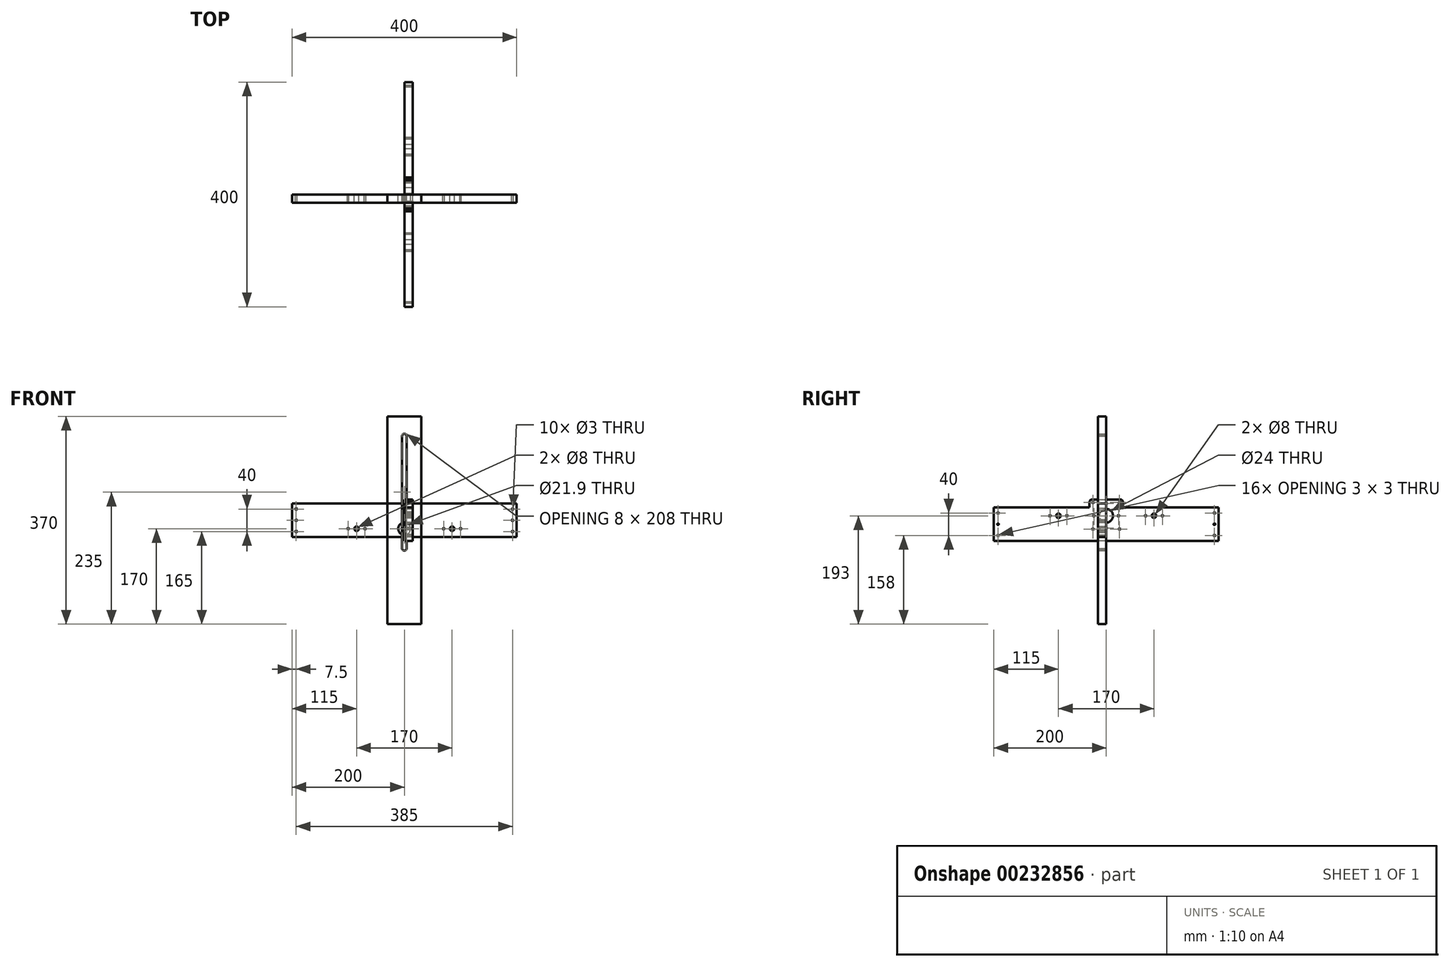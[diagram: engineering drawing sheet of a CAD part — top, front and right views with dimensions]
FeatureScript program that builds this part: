
annotation { "Feature Type Name" : "Feature", "Feature Type Description" : "" }
export const myFeature = defineFeature(function(context is Context, id is Id, definition is map)
    precondition{}
    {
        {
            var Q0;
            Q0=qCreatedBy(makeId("Front.planeOp"),FACE);
            var sketch = newSketch(context, id + "F0", { "sketchPlane" : qUnion([Q0])});
            skLineSegment(sketch, "E0", {"start": v(-200, 30) * mm, "end": v(200, 30) * mm});
            skLineSegment(sketch, "E1", {"start": v(200, 30) * mm, "end": v(200, -30) * mm});
            skLineSegment(sketch, "E2", {"start": v(200, -30) * mm, "end": v(-200, -30) * mm});
            skLineSegment(sketch, "E3", {"start": v(-200, -30) * mm, "end": v(-200, 30) * mm});
            skCircle(sketch, "E4", {"center": v(0, -15) * mm, "radius": 10.95 * mm});
            skCircle(sketch, "E5", {"center": v(-100, -15) * mm, "radius": 1.5 * mm});
            skCircle(sketch, "E6", {"center": v(-70, -15) * mm, "radius": 1.5 * mm});
            skCircle(sketch, "E7", {"center": v(-192.5, -20) * mm, "radius": 1.5 * mm});
            skCircle(sketch, "E8", {"center": v(-192.5, 20) * mm, "radius": 1.5 * mm});
            skCircle(sketch, "E9", {"center": v(-192.5, 0) * mm, "radius": 1.5 * mm});
            skCircle(sketch, "E10", {"center": v(70, -15) * mm, "radius": 1.5 * mm});
            skCircle(sketch, "E11", {"center": v(85, -15) * mm, "radius": 4 * mm});
            skCircle(sketch, "E12", {"center": v(100, -15) * mm, "radius": 1.5 * mm});
            skCircle(sketch, "E13", {"center": v(192.5, -20) * mm, "radius": 1.5 * mm});
            skCircle(sketch, "E14", {"center": v(192.5, 0) * mm, "radius": 1.5 * mm});
            skCircle(sketch, "E15", {"center": v(192.5, 20) * mm, "radius": 1.5 * mm});
            skCircle(sketch, "E16", {"center": v(-85, -15) * mm, "radius": 4 * mm});
            skSolve(sketch);
        }
        {
            var Q0;
            Q0=makeQuery(id+"F0.imprint","IMPRINT",FACE,{"disambiguationData":[TD([[makeQuery(id+"F0.imprint","IMPRINT",EDGE,{"derivedFrom":sQuery(id+"F0.wireOp",EDGE,"E0")}),-1.0]])]});
            extrude(context, id + "F1", {"entities" : qUnion([Q0]), "depth" : 15 * mm});
        }
        {
            var Q0;
            Q0=qCreatedBy(makeId("Right.planeOp"),FACE);
            var sketch = newSketch(context, id + "F2", { "sketchPlane" : qUnion([Q0])});
            skLineSegment(sketch, "E17", {"start": v(-30, 23) * mm, "end": v(-30, 32) * mm});
            skLineSegment(sketch, "E18", {"start": v(-30, 32) * mm, "end": v(-29.96, 32.65) * mm});
            skLineSegment(sketch, "E19", {"start": v(-29.96, 32.65) * mm, "end": v(-29.83, 33.3) * mm});
            skLineSegment(sketch, "E20", {"start": v(-29.83, 33.3) * mm, "end": v(-29.62, 33.91) * mm});
            skLineSegment(sketch, "E21", {"start": v(-29.62, 33.91) * mm, "end": v(-29.33, 34.5) * mm});
            skLineSegment(sketch, "E22", {"start": v(-29.33, 34.5) * mm, "end": v(-28.97, 35.04) * mm});
            skLineSegment(sketch, "E23", {"start": v(-28.97, 35.04) * mm, "end": v(-28.54, 35.54) * mm});
            skLineSegment(sketch, "E24", {"start": v(-28.54, 35.54) * mm, "end": v(-28.04, 35.97) * mm});
            skLineSegment(sketch, "E25", {"start": v(-28.04, 35.97) * mm, "end": v(-27.5, 36.33) * mm});
            skLineSegment(sketch, "E26", {"start": v(-27.5, 36.33) * mm, "end": v(-26.91, 36.62) * mm});
            skLineSegment(sketch, "E27", {"start": v(-26.91, 36.62) * mm, "end": v(-26.3, 36.83) * mm});
            skLineSegment(sketch, "E28", {"start": v(-26.3, 36.83) * mm, "end": v(-25.65, 36.96) * mm});
            skLineSegment(sketch, "E29", {"start": v(-25.65, 36.96) * mm, "end": v(-25, 37) * mm});
            skLineSegment(sketch, "E30", {"start": v(-25, 37) * mm, "end": v(25, 37) * mm});
            skLineSegment(sketch, "E31", {"start": v(25, 37) * mm, "end": v(25.65, 36.96) * mm});
            skLineSegment(sketch, "E32", {"start": v(25.65, 36.96) * mm, "end": v(26.3, 36.83) * mm});
            skLineSegment(sketch, "E33", {"start": v(26.3, 36.83) * mm, "end": v(26.91, 36.62) * mm});
            skLineSegment(sketch, "E34", {"start": v(26.91, 36.62) * mm, "end": v(27.5, 36.33) * mm});
            skLineSegment(sketch, "E35", {"start": v(27.5, 36.33) * mm, "end": v(28.04, 35.97) * mm});
            skLineSegment(sketch, "E36", {"start": v(28.04, 35.97) * mm, "end": v(28.54, 35.54) * mm});
            skLineSegment(sketch, "E37", {"start": v(28.54, 35.54) * mm, "end": v(28.97, 35.04) * mm});
            skLineSegment(sketch, "E38", {"start": v(28.97, 35.04) * mm, "end": v(29.33, 34.5) * mm});
            skLineSegment(sketch, "E39", {"start": v(29.33, 34.5) * mm, "end": v(29.62, 33.91) * mm});
            skLineSegment(sketch, "E40", {"start": v(29.62, 33.91) * mm, "end": v(29.83, 33.3) * mm});
            skLineSegment(sketch, "E41", {"start": v(29.83, 33.3) * mm, "end": v(29.96, 32.65) * mm});
            skLineSegment(sketch, "E42", {"start": v(29.96, 32.65) * mm, "end": v(30, 32) * mm});
            skLineSegment(sketch, "E43", {"start": v(30, 32) * mm, "end": v(30, 23) * mm});
            skLineSegment(sketch, "E44", {"start": v(30, 23) * mm, "end": v(200, 23) * mm});
            skLineSegment(sketch, "E45", {"start": v(200, 23) * mm, "end": v(200, -37) * mm});
            skLineSegment(sketch, "E46", {"start": v(200, -37) * mm, "end": v(-200, -37) * mm});
            skLineSegment(sketch, "E47", {"start": v(-200, -37) * mm, "end": v(-200, 23) * mm});
            skLineSegment(sketch, "E48", {"start": v(-200, 23) * mm, "end": v(-30, 23) * mm});
            skLineSegment(sketch, "E49", {"start": v(-0.39, -12.47) * mm, "end": v(-0.75, -12.62) * mm});
            skLineSegment(sketch, "E50", {"start": v(-0.75, -12.62) * mm, "end": v(-1.06, -12.86) * mm});
            skLineSegment(sketch, "E51", {"start": v(-1.06, -12.86) * mm, "end": v(-1.3, -13.17) * mm});
            skLineSegment(sketch, "E52", {"start": v(-1.3, -13.17) * mm, "end": v(-1.45, -13.53) * mm});
            skLineSegment(sketch, "E53", {"start": v(-1.45, -13.53) * mm, "end": v(-1.5, -13.92) * mm});
            skLineSegment(sketch, "E54", {"start": v(-1.5, -13.92) * mm, "end": v(-1.45, -14.3) * mm});
            skLineSegment(sketch, "E55", {"start": v(-1.45, -14.3) * mm, "end": v(-1.3, -14.67) * mm});
            skLineSegment(sketch, "E56", {"start": v(-1.3, -14.67) * mm, "end": v(-1.06, -14.98) * mm});
            skLineSegment(sketch, "E57", {"start": v(-1.06, -14.98) * mm, "end": v(-0.75, -15.22) * mm});
            skLineSegment(sketch, "E58", {"start": v(-0.75, -15.22) * mm, "end": v(-0.39, -15.37) * mm});
            skLineSegment(sketch, "E59", {"start": v(-0.39, -15.37) * mm, "end": v(0, -15.42) * mm});
            skLineSegment(sketch, "E60", {"start": v(0, -15.42) * mm, "end": v(0.39, -15.37) * mm});
            skLineSegment(sketch, "E61", {"start": v(0.39, -15.37) * mm, "end": v(0.75, -15.22) * mm});
            skLineSegment(sketch, "E62", {"start": v(0.75, -15.22) * mm, "end": v(1.06, -14.98) * mm});
            skLineSegment(sketch, "E63", {"start": v(1.06, -14.98) * mm, "end": v(1.3, -14.67) * mm});
            skLineSegment(sketch, "E64", {"start": v(1.3, -14.67) * mm, "end": v(1.45, -14.3) * mm});
            skLineSegment(sketch, "E65", {"start": v(1.45, -14.3) * mm, "end": v(1.5, -13.92) * mm});
            skLineSegment(sketch, "E66", {"start": v(1.5, -13.92) * mm, "end": v(1.45, -13.53) * mm});
            skLineSegment(sketch, "E67", {"start": v(1.45, -13.53) * mm, "end": v(1.3, -13.17) * mm});
            skLineSegment(sketch, "E68", {"start": v(1.3, -13.17) * mm, "end": v(1.06, -12.86) * mm});
            skLineSegment(sketch, "E69", {"start": v(1.06, -12.86) * mm, "end": v(0.75, -12.62) * mm});
            skLineSegment(sketch, "E70", {"start": v(0.75, -12.62) * mm, "end": v(0.39, -12.47) * mm});
            skLineSegment(sketch, "E71", {"start": v(0.39, -12.47) * mm, "end": v(0, -12.42) * mm});
            skLineSegment(sketch, "E72", {"start": v(0, -12.42) * mm, "end": v(-0.39, -12.47) * mm});
            skLineSegment(sketch, "E73", {"start": v(21.17, 9.3) * mm, "end": v(20.86, 9.06) * mm});
            skLineSegment(sketch, "E74", {"start": v(20.86, 9.06) * mm, "end": v(20.62, 8.75) * mm});
            skLineSegment(sketch, "E75", {"start": v(20.62, 8.75) * mm, "end": v(20.47, 8.39) * mm});
            skLineSegment(sketch, "E76", {"start": v(20.47, 8.39) * mm, "end": v(20.42, 8) * mm});
            skLineSegment(sketch, "E77", {"start": v(20.42, 8) * mm, "end": v(20.47, 7.61) * mm});
            skLineSegment(sketch, "E78", {"start": v(20.47, 7.61) * mm, "end": v(20.62, 7.25) * mm});
            skLineSegment(sketch, "E79", {"start": v(20.62, 7.25) * mm, "end": v(20.86, 6.94) * mm});
            skLineSegment(sketch, "E80", {"start": v(20.86, 6.94) * mm, "end": v(21.17, 6.7) * mm});
            skLineSegment(sketch, "E81", {"start": v(21.17, 6.7) * mm, "end": v(21.53, 6.55) * mm});
            skLineSegment(sketch, "E82", {"start": v(21.53, 6.55) * mm, "end": v(21.92, 6.5) * mm});
            skLineSegment(sketch, "E83", {"start": v(21.92, 6.5) * mm, "end": v(22.3, 6.55) * mm});
            skLineSegment(sketch, "E84", {"start": v(22.3, 6.55) * mm, "end": v(22.67, 6.7) * mm});
            skLineSegment(sketch, "E85", {"start": v(22.67, 6.7) * mm, "end": v(22.98, 6.94) * mm});
            skLineSegment(sketch, "E86", {"start": v(22.98, 6.94) * mm, "end": v(23.22, 7.25) * mm});
            skLineSegment(sketch, "E87", {"start": v(23.22, 7.25) * mm, "end": v(23.37, 7.61) * mm});
            skLineSegment(sketch, "E88", {"start": v(23.37, 7.61) * mm, "end": v(23.42, 8) * mm});
            skLineSegment(sketch, "E89", {"start": v(23.42, 8) * mm, "end": v(23.37, 8.39) * mm});
            skLineSegment(sketch, "E90", {"start": v(23.37, 8.39) * mm, "end": v(23.22, 8.75) * mm});
            skLineSegment(sketch, "E91", {"start": v(23.22, 8.75) * mm, "end": v(22.98, 9.06) * mm});
            skLineSegment(sketch, "E92", {"start": v(22.98, 9.06) * mm, "end": v(22.67, 9.3) * mm});
            skLineSegment(sketch, "E93", {"start": v(22.67, 9.3) * mm, "end": v(22.3, 9.45) * mm});
            skLineSegment(sketch, "E94", {"start": v(22.3, 9.45) * mm, "end": v(21.92, 9.5) * mm});
            skLineSegment(sketch, "E95", {"start": v(21.92, 9.5) * mm, "end": v(21.53, 9.45) * mm});
            skLineSegment(sketch, "E96", {"start": v(21.53, 9.45) * mm, "end": v(21.17, 9.3) * mm});
            skLineSegment(sketch, "E97", {"start": v(-22.98, 9.06) * mm, "end": v(-23.22, 8.75) * mm});
            skLineSegment(sketch, "E98", {"start": v(-23.22, 8.75) * mm, "end": v(-23.37, 8.39) * mm});
            skLineSegment(sketch, "E99", {"start": v(-23.37, 8.39) * mm, "end": v(-23.42, 8) * mm});
            skLineSegment(sketch, "E100", {"start": v(-23.42, 8) * mm, "end": v(-23.37, 7.61) * mm});
            skLineSegment(sketch, "E101", {"start": v(-23.37, 7.61) * mm, "end": v(-23.22, 7.25) * mm});
            skLineSegment(sketch, "E102", {"start": v(-23.22, 7.25) * mm, "end": v(-22.98, 6.94) * mm});
            skLineSegment(sketch, "E103", {"start": v(-22.98, 6.94) * mm, "end": v(-22.67, 6.7) * mm});
            skLineSegment(sketch, "E104", {"start": v(-22.67, 6.7) * mm, "end": v(-22.3, 6.55) * mm});
            skLineSegment(sketch, "E105", {"start": v(-22.3, 6.55) * mm, "end": v(-21.92, 6.5) * mm});
            skLineSegment(sketch, "E106", {"start": v(-21.92, 6.5) * mm, "end": v(-21.53, 6.55) * mm});
            skLineSegment(sketch, "E107", {"start": v(-21.53, 6.55) * mm, "end": v(-21.17, 6.7) * mm});
            skLineSegment(sketch, "E108", {"start": v(-21.17, 6.7) * mm, "end": v(-20.86, 6.94) * mm});
            skLineSegment(sketch, "E109", {"start": v(-20.86, 6.94) * mm, "end": v(-20.62, 7.25) * mm});
            skLineSegment(sketch, "E110", {"start": v(-20.62, 7.25) * mm, "end": v(-20.47, 7.61) * mm});
            skLineSegment(sketch, "E111", {"start": v(-20.47, 7.61) * mm, "end": v(-20.42, 8) * mm});
            skLineSegment(sketch, "E112", {"start": v(-20.42, 8) * mm, "end": v(-20.47, 8.39) * mm});
            skLineSegment(sketch, "E113", {"start": v(-20.47, 8.39) * mm, "end": v(-20.62, 8.75) * mm});
            skLineSegment(sketch, "E114", {"start": v(-20.62, 8.75) * mm, "end": v(-20.86, 9.06) * mm});
            skLineSegment(sketch, "E115", {"start": v(-20.86, 9.06) * mm, "end": v(-21.17, 9.3) * mm});
            skLineSegment(sketch, "E116", {"start": v(-21.17, 9.3) * mm, "end": v(-21.53, 9.45) * mm});
            skLineSegment(sketch, "E117", {"start": v(-21.53, 9.45) * mm, "end": v(-21.92, 9.5) * mm});
            skLineSegment(sketch, "E118", {"start": v(-21.92, 9.5) * mm, "end": v(-22.3, 9.45) * mm});
            skLineSegment(sketch, "E119", {"start": v(-22.3, 9.45) * mm, "end": v(-22.67, 9.3) * mm});
            skLineSegment(sketch, "E120", {"start": v(-22.67, 9.3) * mm, "end": v(-22.98, 9.06) * mm});
            skLineSegment(sketch, "E121", {"start": v(-1.3, 29.17) * mm, "end": v(-1.06, 28.86) * mm});
            skLineSegment(sketch, "E122", {"start": v(-1.06, 28.86) * mm, "end": v(-0.75, 28.62) * mm});
            skLineSegment(sketch, "E123", {"start": v(-0.75, 28.62) * mm, "end": v(-0.39, 28.47) * mm});
            skLineSegment(sketch, "E124", {"start": v(-0.39, 28.47) * mm, "end": v(0, 28.42) * mm});
            skLineSegment(sketch, "E125", {"start": v(0, 28.42) * mm, "end": v(0.39, 28.47) * mm});
            skLineSegment(sketch, "E126", {"start": v(0.39, 28.47) * mm, "end": v(0.75, 28.62) * mm});
            skLineSegment(sketch, "E127", {"start": v(0.75, 28.62) * mm, "end": v(1.06, 28.86) * mm});
            skLineSegment(sketch, "E128", {"start": v(1.06, 28.86) * mm, "end": v(1.3, 29.17) * mm});
            skLineSegment(sketch, "E129", {"start": v(1.3, 29.17) * mm, "end": v(1.45, 29.53) * mm});
            skLineSegment(sketch, "E130", {"start": v(1.45, 29.53) * mm, "end": v(1.5, 29.92) * mm});
            skLineSegment(sketch, "E131", {"start": v(1.5, 29.92) * mm, "end": v(1.45, 30.3) * mm});
            skLineSegment(sketch, "E132", {"start": v(1.45, 30.3) * mm, "end": v(1.3, 30.67) * mm});
            skLineSegment(sketch, "E133", {"start": v(1.3, 30.67) * mm, "end": v(1.06, 30.98) * mm});
            skLineSegment(sketch, "E134", {"start": v(1.06, 30.98) * mm, "end": v(0.75, 31.22) * mm});
            skLineSegment(sketch, "E135", {"start": v(0.75, 31.22) * mm, "end": v(0.39, 31.37) * mm});
            skLineSegment(sketch, "E136", {"start": v(0.39, 31.37) * mm, "end": v(0, 31.42) * mm});
            skLineSegment(sketch, "E137", {"start": v(0, 31.42) * mm, "end": v(-0.39, 31.37) * mm});
            skLineSegment(sketch, "E138", {"start": v(-0.39, 31.37) * mm, "end": v(-0.75, 31.22) * mm});
            skLineSegment(sketch, "E139", {"start": v(-0.75, 31.22) * mm, "end": v(-1.06, 30.98) * mm});
            skLineSegment(sketch, "E140", {"start": v(-1.06, 30.98) * mm, "end": v(-1.3, 30.67) * mm});
            skLineSegment(sketch, "E141", {"start": v(-1.3, 30.67) * mm, "end": v(-1.45, 30.3) * mm});
            skLineSegment(sketch, "E142", {"start": v(-1.45, 30.3) * mm, "end": v(-1.5, 29.92) * mm});
            skLineSegment(sketch, "E143", {"start": v(-1.5, 29.92) * mm, "end": v(-1.45, 29.53) * mm});
            skLineSegment(sketch, "E144", {"start": v(-1.45, 29.53) * mm, "end": v(-1.3, 29.17) * mm});
            skLineSegment(sketch, "E145", {"start": v(23.94, -14.1) * mm, "end": v(23.55, -14.05) * mm});
            skLineSegment(sketch, "E146", {"start": v(23.55, -14.05) * mm, "end": v(23.16, -14.1) * mm});
            skLineSegment(sketch, "E147", {"start": v(23.16, -14.1) * mm, "end": v(22.8, -14.25) * mm});
            skLineSegment(sketch, "E148", {"start": v(22.8, -14.25) * mm, "end": v(22.49, -14.49) * mm});
            skLineSegment(sketch, "E149", {"start": v(22.49, -14.49) * mm, "end": v(22.25, -14.8) * mm});
            skLineSegment(sketch, "E150", {"start": v(22.25, -14.8) * mm, "end": v(22.1, -15.16) * mm});
            skLineSegment(sketch, "E151", {"start": v(22.1, -15.16) * mm, "end": v(22.05, -15.55) * mm});
            skLineSegment(sketch, "E152", {"start": v(22.05, -15.55) * mm, "end": v(22.1, -15.94) * mm});
            skLineSegment(sketch, "E153", {"start": v(22.1, -15.94) * mm, "end": v(22.25, -16.3) * mm});
            skLineSegment(sketch, "E154", {"start": v(22.25, -16.3) * mm, "end": v(22.49, -16.61) * mm});
            skLineSegment(sketch, "E155", {"start": v(22.49, -16.61) * mm, "end": v(22.8, -16.85) * mm});
            skLineSegment(sketch, "E156", {"start": v(22.8, -16.85) * mm, "end": v(23.16, -17) * mm});
            skLineSegment(sketch, "E157", {"start": v(23.16, -17) * mm, "end": v(23.55, -17.05) * mm});
            skLineSegment(sketch, "E158", {"start": v(23.55, -17.05) * mm, "end": v(23.94, -17) * mm});
            skLineSegment(sketch, "E159", {"start": v(23.94, -17) * mm, "end": v(24.3, -16.85) * mm});
            skLineSegment(sketch, "E160", {"start": v(24.3, -16.85) * mm, "end": v(24.61, -16.61) * mm});
            skLineSegment(sketch, "E161", {"start": v(24.61, -16.61) * mm, "end": v(24.85, -16.3) * mm});
            skLineSegment(sketch, "E162", {"start": v(24.85, -16.3) * mm, "end": v(25, -15.94) * mm});
            skLineSegment(sketch, "E163", {"start": v(25, -15.94) * mm, "end": v(25.05, -15.55) * mm});
            skLineSegment(sketch, "E164", {"start": v(25.05, -15.55) * mm, "end": v(25, -15.16) * mm});
            skLineSegment(sketch, "E165", {"start": v(25, -15.16) * mm, "end": v(24.85, -14.8) * mm});
            skLineSegment(sketch, "E166", {"start": v(24.85, -14.8) * mm, "end": v(24.61, -14.49) * mm});
            skLineSegment(sketch, "E167", {"start": v(24.61, -14.49) * mm, "end": v(24.3, -14.25) * mm});
            skLineSegment(sketch, "E168", {"start": v(24.3, -14.25) * mm, "end": v(23.94, -14.1) * mm});
            skLineSegment(sketch, "E169", {"start": v(-25, -15.94) * mm, "end": v(-24.85, -16.3) * mm});
            skLineSegment(sketch, "E170", {"start": v(-24.85, -16.3) * mm, "end": v(-24.61, -16.61) * mm});
            skLineSegment(sketch, "E171", {"start": v(-24.61, -16.61) * mm, "end": v(-24.3, -16.85) * mm});
            skLineSegment(sketch, "E172", {"start": v(-24.3, -16.85) * mm, "end": v(-23.94, -17) * mm});
            skLineSegment(sketch, "E173", {"start": v(-23.94, -17) * mm, "end": v(-23.55, -17.05) * mm});
            skLineSegment(sketch, "E174", {"start": v(-23.55, -17.05) * mm, "end": v(-23.16, -17) * mm});
            skLineSegment(sketch, "E175", {"start": v(-23.16, -17) * mm, "end": v(-22.8, -16.85) * mm});
            skLineSegment(sketch, "E176", {"start": v(-22.8, -16.85) * mm, "end": v(-22.49, -16.61) * mm});
            skLineSegment(sketch, "E177", {"start": v(-22.49, -16.61) * mm, "end": v(-22.25, -16.3) * mm});
            skLineSegment(sketch, "E178", {"start": v(-22.25, -16.3) * mm, "end": v(-22.1, -15.94) * mm});
            skLineSegment(sketch, "E179", {"start": v(-22.1, -15.94) * mm, "end": v(-22.05, -15.55) * mm});
            skLineSegment(sketch, "E180", {"start": v(-22.05, -15.55) * mm, "end": v(-22.1, -15.16) * mm});
            skLineSegment(sketch, "E181", {"start": v(-22.1, -15.16) * mm, "end": v(-22.25, -14.8) * mm});
            skLineSegment(sketch, "E182", {"start": v(-22.25, -14.8) * mm, "end": v(-22.49, -14.49) * mm});
            skLineSegment(sketch, "E183", {"start": v(-22.49, -14.49) * mm, "end": v(-22.8, -14.25) * mm});
            skLineSegment(sketch, "E184", {"start": v(-22.8, -14.25) * mm, "end": v(-23.16, -14.1) * mm});
            skLineSegment(sketch, "E185", {"start": v(-23.16, -14.1) * mm, "end": v(-23.55, -14.05) * mm});
            skLineSegment(sketch, "E186", {"start": v(-23.55, -14.05) * mm, "end": v(-23.94, -14.1) * mm});
            skLineSegment(sketch, "E187", {"start": v(-23.94, -14.1) * mm, "end": v(-24.3, -14.25) * mm});
            skLineSegment(sketch, "E188", {"start": v(-24.3, -14.25) * mm, "end": v(-24.61, -14.49) * mm});
            skLineSegment(sketch, "E189", {"start": v(-24.61, -14.49) * mm, "end": v(-24.85, -14.8) * mm});
            skLineSegment(sketch, "E190", {"start": v(-24.85, -14.8) * mm, "end": v(-25, -15.16) * mm});
            skLineSegment(sketch, "E191", {"start": v(-25, -15.16) * mm, "end": v(-25.05, -15.55) * mm});
            skLineSegment(sketch, "E192", {"start": v(-25.05, -15.55) * mm, "end": v(-25, -15.94) * mm});
            skLineSegment(sketch, "E193", {"start": v(-22.1, 31.16) * mm, "end": v(-22.05, 31.55) * mm});
            skLineSegment(sketch, "E194", {"start": v(-22.05, 31.55) * mm, "end": v(-22.1, 31.94) * mm});
            skLineSegment(sketch, "E195", {"start": v(-22.1, 31.94) * mm, "end": v(-22.25, 32.3) * mm});
            skLineSegment(sketch, "E196", {"start": v(-22.25, 32.3) * mm, "end": v(-22.49, 32.61) * mm});
            skLineSegment(sketch, "E197", {"start": v(-22.49, 32.61) * mm, "end": v(-22.8, 32.85) * mm});
            skLineSegment(sketch, "E198", {"start": v(-22.8, 32.85) * mm, "end": v(-23.16, 33) * mm});
            skLineSegment(sketch, "E199", {"start": v(-23.16, 33) * mm, "end": v(-23.55, 33.05) * mm});
            skLineSegment(sketch, "E200", {"start": v(-23.55, 33.05) * mm, "end": v(-23.94, 33) * mm});
            skLineSegment(sketch, "E201", {"start": v(-23.94, 33) * mm, "end": v(-24.3, 32.85) * mm});
            skLineSegment(sketch, "E202", {"start": v(-24.3, 32.85) * mm, "end": v(-24.61, 32.61) * mm});
            skLineSegment(sketch, "E203", {"start": v(-24.61, 32.61) * mm, "end": v(-24.85, 32.3) * mm});
            skLineSegment(sketch, "E204", {"start": v(-24.85, 32.3) * mm, "end": v(-25, 31.94) * mm});
            skLineSegment(sketch, "E205", {"start": v(-25, 31.94) * mm, "end": v(-25.05, 31.55) * mm});
            skLineSegment(sketch, "E206", {"start": v(-25.05, 31.55) * mm, "end": v(-25, 31.16) * mm});
            skLineSegment(sketch, "E207", {"start": v(-25, 31.16) * mm, "end": v(-24.85, 30.8) * mm});
            skLineSegment(sketch, "E208", {"start": v(-24.85, 30.8) * mm, "end": v(-24.61, 30.49) * mm});
            skLineSegment(sketch, "E209", {"start": v(-24.61, 30.49) * mm, "end": v(-24.3, 30.25) * mm});
            skLineSegment(sketch, "E210", {"start": v(-24.3, 30.25) * mm, "end": v(-23.94, 30.1) * mm});
            skLineSegment(sketch, "E211", {"start": v(-23.94, 30.1) * mm, "end": v(-23.55, 30.05) * mm});
            skLineSegment(sketch, "E212", {"start": v(-23.55, 30.05) * mm, "end": v(-23.16, 30.1) * mm});
            skLineSegment(sketch, "E213", {"start": v(-23.16, 30.1) * mm, "end": v(-22.8, 30.25) * mm});
            skLineSegment(sketch, "E214", {"start": v(-22.8, 30.25) * mm, "end": v(-22.49, 30.49) * mm});
            skLineSegment(sketch, "E215", {"start": v(-22.49, 30.49) * mm, "end": v(-22.25, 30.8) * mm});
            skLineSegment(sketch, "E216", {"start": v(-22.25, 30.8) * mm, "end": v(-22.1, 31.16) * mm});
            skLineSegment(sketch, "E217", {"start": v(24.3, 30.25) * mm, "end": v(24.61, 30.49) * mm});
            skLineSegment(sketch, "E218", {"start": v(24.61, 30.49) * mm, "end": v(24.85, 30.8) * mm});
            skLineSegment(sketch, "E219", {"start": v(24.85, 30.8) * mm, "end": v(25, 31.16) * mm});
            skLineSegment(sketch, "E220", {"start": v(25, 31.16) * mm, "end": v(25.05, 31.55) * mm});
            skLineSegment(sketch, "E221", {"start": v(25.05, 31.55) * mm, "end": v(25, 31.94) * mm});
            skLineSegment(sketch, "E222", {"start": v(25, 31.94) * mm, "end": v(24.85, 32.3) * mm});
            skLineSegment(sketch, "E223", {"start": v(24.85, 32.3) * mm, "end": v(24.61, 32.61) * mm});
            skLineSegment(sketch, "E224", {"start": v(24.61, 32.61) * mm, "end": v(24.3, 32.85) * mm});
            skLineSegment(sketch, "E225", {"start": v(24.3, 32.85) * mm, "end": v(23.94, 33) * mm});
            skLineSegment(sketch, "E226", {"start": v(23.94, 33) * mm, "end": v(23.55, 33.05) * mm});
            skLineSegment(sketch, "E227", {"start": v(23.55, 33.05) * mm, "end": v(23.16, 33) * mm});
            skLineSegment(sketch, "E228", {"start": v(23.16, 33) * mm, "end": v(22.8, 32.85) * mm});
            skLineSegment(sketch, "E229", {"start": v(22.8, 32.85) * mm, "end": v(22.49, 32.61) * mm});
            skLineSegment(sketch, "E230", {"start": v(22.49, 32.61) * mm, "end": v(22.25, 32.3) * mm});
            skLineSegment(sketch, "E231", {"start": v(22.25, 32.3) * mm, "end": v(22.1, 31.94) * mm});
            skLineSegment(sketch, "E232", {"start": v(22.1, 31.94) * mm, "end": v(22.05, 31.55) * mm});
            skLineSegment(sketch, "E233", {"start": v(22.05, 31.55) * mm, "end": v(22.1, 31.16) * mm});
            skLineSegment(sketch, "E234", {"start": v(22.1, 31.16) * mm, "end": v(22.25, 30.8) * mm});
            skLineSegment(sketch, "E235", {"start": v(22.25, 30.8) * mm, "end": v(22.49, 30.49) * mm});
            skLineSegment(sketch, "E236", {"start": v(22.49, 30.49) * mm, "end": v(22.8, 30.25) * mm});
            skLineSegment(sketch, "E237", {"start": v(22.8, 30.25) * mm, "end": v(23.16, 30.1) * mm});
            skLineSegment(sketch, "E238", {"start": v(23.16, 30.1) * mm, "end": v(23.55, 30.05) * mm});
            skLineSegment(sketch, "E239", {"start": v(23.55, 30.05) * mm, "end": v(23.94, 30.1) * mm});
            skLineSegment(sketch, "E240", {"start": v(23.94, 30.1) * mm, "end": v(24.3, 30.25) * mm});
            skLineSegment(sketch, "E241", {"start": v(192.11, 14.45) * mm, "end": v(191.75, 14.3) * mm});
            skLineSegment(sketch, "E242", {"start": v(191.75, 14.3) * mm, "end": v(191.44, 14.06) * mm});
            skLineSegment(sketch, "E243", {"start": v(191.44, 14.06) * mm, "end": v(191.2, 13.75) * mm});
            skLineSegment(sketch, "E244", {"start": v(191.2, 13.75) * mm, "end": v(191.05, 13.39) * mm});
            skLineSegment(sketch, "E245", {"start": v(191.05, 13.39) * mm, "end": v(191, 13) * mm});
            skLineSegment(sketch, "E246", {"start": v(191, 13) * mm, "end": v(191.05, 12.61) * mm});
            skLineSegment(sketch, "E247", {"start": v(191.05, 12.61) * mm, "end": v(191.2, 12.25) * mm});
            skLineSegment(sketch, "E248", {"start": v(191.2, 12.25) * mm, "end": v(191.44, 11.94) * mm});
            skLineSegment(sketch, "E249", {"start": v(191.44, 11.94) * mm, "end": v(191.75, 11.7) * mm});
            skLineSegment(sketch, "E250", {"start": v(191.75, 11.7) * mm, "end": v(192.11, 11.55) * mm});
            skLineSegment(sketch, "E251", {"start": v(192.11, 11.55) * mm, "end": v(192.5, 11.5) * mm});
            skLineSegment(sketch, "E252", {"start": v(192.5, 11.5) * mm, "end": v(192.89, 11.55) * mm});
            skLineSegment(sketch, "E253", {"start": v(192.89, 11.55) * mm, "end": v(193.25, 11.7) * mm});
            skLineSegment(sketch, "E254", {"start": v(193.25, 11.7) * mm, "end": v(193.56, 11.94) * mm});
            skLineSegment(sketch, "E255", {"start": v(193.56, 11.94) * mm, "end": v(193.8, 12.25) * mm});
            skLineSegment(sketch, "E256", {"start": v(193.8, 12.25) * mm, "end": v(193.95, 12.61) * mm});
            skLineSegment(sketch, "E257", {"start": v(193.95, 12.61) * mm, "end": v(194, 13) * mm});
            skLineSegment(sketch, "E258", {"start": v(194, 13) * mm, "end": v(193.95, 13.39) * mm});
            skLineSegment(sketch, "E259", {"start": v(193.95, 13.39) * mm, "end": v(193.8, 13.75) * mm});
            skLineSegment(sketch, "E260", {"start": v(193.8, 13.75) * mm, "end": v(193.56, 14.06) * mm});
            skLineSegment(sketch, "E261", {"start": v(193.56, 14.06) * mm, "end": v(193.25, 14.3) * mm});
            skLineSegment(sketch, "E262", {"start": v(193.25, 14.3) * mm, "end": v(192.89, 14.45) * mm});
            skLineSegment(sketch, "E263", {"start": v(192.89, 14.45) * mm, "end": v(192.5, 14.5) * mm});
            skLineSegment(sketch, "E264", {"start": v(192.5, 14.5) * mm, "end": v(192.11, 14.45) * mm});
            skLineSegment(sketch, "E265", {"start": v(191, -27) * mm, "end": v(191.05, -27.39) * mm});
            skLineSegment(sketch, "E266", {"start": v(191.05, -27.39) * mm, "end": v(191.2, -27.75) * mm});
            skLineSegment(sketch, "E267", {"start": v(191.2, -27.75) * mm, "end": v(191.44, -28.06) * mm});
            skLineSegment(sketch, "E268", {"start": v(191.44, -28.06) * mm, "end": v(191.75, -28.3) * mm});
            skLineSegment(sketch, "E269", {"start": v(191.75, -28.3) * mm, "end": v(192.11, -28.45) * mm});
            skLineSegment(sketch, "E270", {"start": v(192.11, -28.45) * mm, "end": v(192.5, -28.5) * mm});
            skLineSegment(sketch, "E271", {"start": v(192.5, -28.5) * mm, "end": v(192.89, -28.45) * mm});
            skLineSegment(sketch, "E272", {"start": v(192.89, -28.45) * mm, "end": v(193.25, -28.3) * mm});
            skLineSegment(sketch, "E273", {"start": v(193.25, -28.3) * mm, "end": v(193.56, -28.06) * mm});
            skLineSegment(sketch, "E274", {"start": v(193.56, -28.06) * mm, "end": v(193.8, -27.75) * mm});
            skLineSegment(sketch, "E275", {"start": v(193.8, -27.75) * mm, "end": v(193.95, -27.39) * mm});
            skLineSegment(sketch, "E276", {"start": v(193.95, -27.39) * mm, "end": v(194, -27) * mm});
            skLineSegment(sketch, "E277", {"start": v(194, -27) * mm, "end": v(193.95, -26.61) * mm});
            skLineSegment(sketch, "E278", {"start": v(193.95, -26.61) * mm, "end": v(193.8, -26.25) * mm});
            skLineSegment(sketch, "E279", {"start": v(193.8, -26.25) * mm, "end": v(193.56, -25.94) * mm});
            skLineSegment(sketch, "E280", {"start": v(193.56, -25.94) * mm, "end": v(193.25, -25.7) * mm});
            skLineSegment(sketch, "E281", {"start": v(193.25, -25.7) * mm, "end": v(192.89, -25.55) * mm});
            skLineSegment(sketch, "E282", {"start": v(192.89, -25.55) * mm, "end": v(192.5, -25.5) * mm});
            skLineSegment(sketch, "E283", {"start": v(192.5, -25.5) * mm, "end": v(192.11, -25.55) * mm});
            skLineSegment(sketch, "E284", {"start": v(192.11, -25.55) * mm, "end": v(191.75, -25.7) * mm});
            skLineSegment(sketch, "E285", {"start": v(191.75, -25.7) * mm, "end": v(191.44, -25.94) * mm});
            skLineSegment(sketch, "E286", {"start": v(191.44, -25.94) * mm, "end": v(191.2, -26.25) * mm});
            skLineSegment(sketch, "E287", {"start": v(191.2, -26.25) * mm, "end": v(191.05, -26.61) * mm});
            skLineSegment(sketch, "E288", {"start": v(191.05, -26.61) * mm, "end": v(191, -27) * mm});
            skLineSegment(sketch, "E289", {"start": v(-191.44, 11.94) * mm, "end": v(-191.2, 12.25) * mm});
            skLineSegment(sketch, "E290", {"start": v(-191.2, 12.25) * mm, "end": v(-191.05, 12.61) * mm});
            skLineSegment(sketch, "E291", {"start": v(-191.05, 12.61) * mm, "end": v(-191, 13) * mm});
            skLineSegment(sketch, "E292", {"start": v(-191, 13) * mm, "end": v(-191.05, 13.39) * mm});
            skLineSegment(sketch, "E293", {"start": v(-191.05, 13.39) * mm, "end": v(-191.2, 13.75) * mm});
            skLineSegment(sketch, "E294", {"start": v(-191.2, 13.75) * mm, "end": v(-191.44, 14.06) * mm});
            skLineSegment(sketch, "E295", {"start": v(-191.44, 14.06) * mm, "end": v(-191.75, 14.3) * mm});
            skLineSegment(sketch, "E296", {"start": v(-191.75, 14.3) * mm, "end": v(-192.11, 14.45) * mm});
            skLineSegment(sketch, "E297", {"start": v(-192.11, 14.45) * mm, "end": v(-192.5, 14.5) * mm});
            skLineSegment(sketch, "E298", {"start": v(-192.5, 14.5) * mm, "end": v(-192.89, 14.45) * mm});
            skLineSegment(sketch, "E299", {"start": v(-192.89, 14.45) * mm, "end": v(-193.25, 14.3) * mm});
            skLineSegment(sketch, "E300", {"start": v(-193.25, 14.3) * mm, "end": v(-193.56, 14.06) * mm});
            skLineSegment(sketch, "E301", {"start": v(-193.56, 14.06) * mm, "end": v(-193.8, 13.75) * mm});
            skLineSegment(sketch, "E302", {"start": v(-193.8, 13.75) * mm, "end": v(-193.95, 13.39) * mm});
            skLineSegment(sketch, "E303", {"start": v(-193.95, 13.39) * mm, "end": v(-194, 13) * mm});
            skLineSegment(sketch, "E304", {"start": v(-194, 13) * mm, "end": v(-193.95, 12.61) * mm});
            skLineSegment(sketch, "E305", {"start": v(-193.95, 12.61) * mm, "end": v(-193.8, 12.25) * mm});
            skLineSegment(sketch, "E306", {"start": v(-193.8, 12.25) * mm, "end": v(-193.56, 11.94) * mm});
            skLineSegment(sketch, "E307", {"start": v(-193.56, 11.94) * mm, "end": v(-193.25, 11.7) * mm});
            skLineSegment(sketch, "E308", {"start": v(-193.25, 11.7) * mm, "end": v(-192.89, 11.55) * mm});
            skLineSegment(sketch, "E309", {"start": v(-192.89, 11.55) * mm, "end": v(-192.5, 11.5) * mm});
            skLineSegment(sketch, "E310", {"start": v(-192.5, 11.5) * mm, "end": v(-192.11, 11.55) * mm});
            skLineSegment(sketch, "E311", {"start": v(-192.11, 11.55) * mm, "end": v(-191.75, 11.7) * mm});
            skLineSegment(sketch, "E312", {"start": v(-191.75, 11.7) * mm, "end": v(-191.44, 11.94) * mm});
            skLineSegment(sketch, "E313", {"start": v(-193.56, -25.94) * mm, "end": v(-193.8, -26.25) * mm});
            skLineSegment(sketch, "E314", {"start": v(-193.8, -26.25) * mm, "end": v(-193.95, -26.61) * mm});
            skLineSegment(sketch, "E315", {"start": v(-193.95, -26.61) * mm, "end": v(-194, -27) * mm});
            skLineSegment(sketch, "E316", {"start": v(-194, -27) * mm, "end": v(-193.95, -27.39) * mm});
            skLineSegment(sketch, "E317", {"start": v(-193.95, -27.39) * mm, "end": v(-193.8, -27.75) * mm});
            skLineSegment(sketch, "E318", {"start": v(-193.8, -27.75) * mm, "end": v(-193.56, -28.06) * mm});
            skLineSegment(sketch, "E319", {"start": v(-193.56, -28.06) * mm, "end": v(-193.25, -28.3) * mm});
            skLineSegment(sketch, "E320", {"start": v(-193.25, -28.3) * mm, "end": v(-192.89, -28.45) * mm});
            skLineSegment(sketch, "E321", {"start": v(-192.89, -28.45) * mm, "end": v(-192.5, -28.5) * mm});
            skLineSegment(sketch, "E322", {"start": v(-192.5, -28.5) * mm, "end": v(-192.11, -28.45) * mm});
            skLineSegment(sketch, "E323", {"start": v(-192.11, -28.45) * mm, "end": v(-191.75, -28.3) * mm});
            skLineSegment(sketch, "E324", {"start": v(-191.75, -28.3) * mm, "end": v(-191.44, -28.06) * mm});
            skLineSegment(sketch, "E325", {"start": v(-191.44, -28.06) * mm, "end": v(-191.2, -27.75) * mm});
            skLineSegment(sketch, "E326", {"start": v(-191.2, -27.75) * mm, "end": v(-191.05, -27.39) * mm});
            skLineSegment(sketch, "E327", {"start": v(-191.05, -27.39) * mm, "end": v(-191, -27) * mm});
            skLineSegment(sketch, "E328", {"start": v(-191, -27) * mm, "end": v(-191.05, -26.61) * mm});
            skLineSegment(sketch, "E329", {"start": v(-191.05, -26.61) * mm, "end": v(-191.2, -26.25) * mm});
            skLineSegment(sketch, "E330", {"start": v(-191.2, -26.25) * mm, "end": v(-191.44, -25.94) * mm});
            skLineSegment(sketch, "E331", {"start": v(-191.44, -25.94) * mm, "end": v(-191.75, -25.7) * mm});
            skLineSegment(sketch, "E332", {"start": v(-191.75, -25.7) * mm, "end": v(-192.11, -25.55) * mm});
            skLineSegment(sketch, "E333", {"start": v(-192.11, -25.55) * mm, "end": v(-192.5, -25.5) * mm});
            skLineSegment(sketch, "E334", {"start": v(-192.5, -25.5) * mm, "end": v(-192.89, -25.55) * mm});
            skLineSegment(sketch, "E335", {"start": v(-192.89, -25.55) * mm, "end": v(-193.25, -25.7) * mm});
            skLineSegment(sketch, "E336", {"start": v(-193.25, -25.7) * mm, "end": v(-193.56, -25.94) * mm});
            skLineSegment(sketch, "E337", {"start": v(101.5, 8) * mm, "end": v(101.45, 8.39) * mm});
            skLineSegment(sketch, "E338", {"start": v(101.45, 8.39) * mm, "end": v(101.3, 8.75) * mm});
            skLineSegment(sketch, "E339", {"start": v(101.3, 8.75) * mm, "end": v(101.06, 9.06) * mm});
            skLineSegment(sketch, "E340", {"start": v(101.06, 9.06) * mm, "end": v(100.75, 9.3) * mm});
            skLineSegment(sketch, "E341", {"start": v(100.75, 9.3) * mm, "end": v(100.39, 9.45) * mm});
            skLineSegment(sketch, "E342", {"start": v(100.39, 9.45) * mm, "end": v(100, 9.5) * mm});
            skLineSegment(sketch, "E343", {"start": v(100, 9.5) * mm, "end": v(99.61, 9.45) * mm});
            skLineSegment(sketch, "E344", {"start": v(99.61, 9.45) * mm, "end": v(99.25, 9.3) * mm});
            skLineSegment(sketch, "E345", {"start": v(99.25, 9.3) * mm, "end": v(98.94, 9.06) * mm});
            skLineSegment(sketch, "E346", {"start": v(98.94, 9.06) * mm, "end": v(98.7, 8.75) * mm});
            skLineSegment(sketch, "E347", {"start": v(98.7, 8.75) * mm, "end": v(98.55, 8.39) * mm});
            skLineSegment(sketch, "E348", {"start": v(98.55, 8.39) * mm, "end": v(98.5, 8) * mm});
            skLineSegment(sketch, "E349", {"start": v(98.5, 8) * mm, "end": v(98.55, 7.61) * mm});
            skLineSegment(sketch, "E350", {"start": v(98.55, 7.61) * mm, "end": v(98.7, 7.25) * mm});
            skLineSegment(sketch, "E351", {"start": v(98.7, 7.25) * mm, "end": v(98.94, 6.94) * mm});
            skLineSegment(sketch, "E352", {"start": v(98.94, 6.94) * mm, "end": v(99.25, 6.7) * mm});
            skLineSegment(sketch, "E353", {"start": v(99.25, 6.7) * mm, "end": v(99.61, 6.55) * mm});
            skLineSegment(sketch, "E354", {"start": v(99.61, 6.55) * mm, "end": v(100, 6.5) * mm});
            skLineSegment(sketch, "E355", {"start": v(100, 6.5) * mm, "end": v(100.39, 6.55) * mm});
            skLineSegment(sketch, "E356", {"start": v(100.39, 6.55) * mm, "end": v(100.75, 6.7) * mm});
            skLineSegment(sketch, "E357", {"start": v(100.75, 6.7) * mm, "end": v(101.06, 6.94) * mm});
            skLineSegment(sketch, "E358", {"start": v(101.06, 6.94) * mm, "end": v(101.3, 7.25) * mm});
            skLineSegment(sketch, "E359", {"start": v(101.3, 7.25) * mm, "end": v(101.45, 7.61) * mm});
            skLineSegment(sketch, "E360", {"start": v(101.45, 7.61) * mm, "end": v(101.5, 8) * mm});
            skLineSegment(sketch, "E361", {"start": v(70.39, 6.55) * mm, "end": v(70.75, 6.7) * mm});
            skLineSegment(sketch, "E362", {"start": v(70.75, 6.7) * mm, "end": v(71.06, 6.94) * mm});
            skLineSegment(sketch, "E363", {"start": v(71.06, 6.94) * mm, "end": v(71.3, 7.25) * mm});
            skLineSegment(sketch, "E364", {"start": v(71.3, 7.25) * mm, "end": v(71.45, 7.61) * mm});
            skLineSegment(sketch, "E365", {"start": v(71.45, 7.61) * mm, "end": v(71.5, 8) * mm});
            skLineSegment(sketch, "E366", {"start": v(71.5, 8) * mm, "end": v(71.45, 8.39) * mm});
            skLineSegment(sketch, "E367", {"start": v(71.45, 8.39) * mm, "end": v(71.3, 8.75) * mm});
            skLineSegment(sketch, "E368", {"start": v(71.3, 8.75) * mm, "end": v(71.06, 9.06) * mm});
            skLineSegment(sketch, "E369", {"start": v(71.06, 9.06) * mm, "end": v(70.75, 9.3) * mm});
            skLineSegment(sketch, "E370", {"start": v(70.75, 9.3) * mm, "end": v(70.39, 9.45) * mm});
            skLineSegment(sketch, "E371", {"start": v(70.39, 9.45) * mm, "end": v(70, 9.5) * mm});
            skLineSegment(sketch, "E372", {"start": v(70, 9.5) * mm, "end": v(69.61, 9.45) * mm});
            skLineSegment(sketch, "E373", {"start": v(69.61, 9.45) * mm, "end": v(69.25, 9.3) * mm});
            skLineSegment(sketch, "E374", {"start": v(69.25, 9.3) * mm, "end": v(68.94, 9.06) * mm});
            skLineSegment(sketch, "E375", {"start": v(68.94, 9.06) * mm, "end": v(68.7, 8.75) * mm});
            skLineSegment(sketch, "E376", {"start": v(68.7, 8.75) * mm, "end": v(68.55, 8.39) * mm});
            skLineSegment(sketch, "E377", {"start": v(68.55, 8.39) * mm, "end": v(68.5, 8) * mm});
            skLineSegment(sketch, "E378", {"start": v(68.5, 8) * mm, "end": v(68.55, 7.61) * mm});
            skLineSegment(sketch, "E379", {"start": v(68.55, 7.61) * mm, "end": v(68.7, 7.25) * mm});
            skLineSegment(sketch, "E380", {"start": v(68.7, 7.25) * mm, "end": v(68.94, 6.94) * mm});
            skLineSegment(sketch, "E381", {"start": v(68.94, 6.94) * mm, "end": v(69.25, 6.7) * mm});
            skLineSegment(sketch, "E382", {"start": v(69.25, 6.7) * mm, "end": v(69.61, 6.55) * mm});
            skLineSegment(sketch, "E383", {"start": v(69.61, 6.55) * mm, "end": v(70, 6.5) * mm});
            skLineSegment(sketch, "E384", {"start": v(70, 6.5) * mm, "end": v(70.39, 6.55) * mm});
            skLineSegment(sketch, "E385", {"start": v(-71.5, 8) * mm, "end": v(-71.45, 7.61) * mm});
            skLineSegment(sketch, "E386", {"start": v(-71.45, 7.61) * mm, "end": v(-71.3, 7.25) * mm});
            skLineSegment(sketch, "E387", {"start": v(-71.3, 7.25) * mm, "end": v(-71.06, 6.94) * mm});
            skLineSegment(sketch, "E388", {"start": v(-71.06, 6.94) * mm, "end": v(-70.75, 6.7) * mm});
            skLineSegment(sketch, "E389", {"start": v(-70.75, 6.7) * mm, "end": v(-70.39, 6.55) * mm});
            skLineSegment(sketch, "E390", {"start": v(-70.39, 6.55) * mm, "end": v(-70, 6.5) * mm});
            skLineSegment(sketch, "E391", {"start": v(-70, 6.5) * mm, "end": v(-69.61, 6.55) * mm});
            skLineSegment(sketch, "E392", {"start": v(-69.61, 6.55) * mm, "end": v(-69.25, 6.7) * mm});
            skLineSegment(sketch, "E393", {"start": v(-69.25, 6.7) * mm, "end": v(-68.94, 6.94) * mm});
            skLineSegment(sketch, "E394", {"start": v(-68.94, 6.94) * mm, "end": v(-68.7, 7.25) * mm});
            skLineSegment(sketch, "E395", {"start": v(-68.7, 7.25) * mm, "end": v(-68.55, 7.61) * mm});
            skLineSegment(sketch, "E396", {"start": v(-68.55, 7.61) * mm, "end": v(-68.5, 8) * mm});
            skLineSegment(sketch, "E397", {"start": v(-68.5, 8) * mm, "end": v(-68.55, 8.39) * mm});
            skLineSegment(sketch, "E398", {"start": v(-68.55, 8.39) * mm, "end": v(-68.7, 8.75) * mm});
            skLineSegment(sketch, "E399", {"start": v(-68.7, 8.75) * mm, "end": v(-68.94, 9.06) * mm});
            skLineSegment(sketch, "E400", {"start": v(-68.94, 9.06) * mm, "end": v(-69.25, 9.3) * mm});
            skLineSegment(sketch, "E401", {"start": v(-69.25, 9.3) * mm, "end": v(-69.61, 9.45) * mm});
            skLineSegment(sketch, "E402", {"start": v(-69.61, 9.45) * mm, "end": v(-70, 9.5) * mm});
            skLineSegment(sketch, "E403", {"start": v(-70, 9.5) * mm, "end": v(-70.39, 9.45) * mm});
            skLineSegment(sketch, "E404", {"start": v(-70.39, 9.45) * mm, "end": v(-70.75, 9.3) * mm});
            skLineSegment(sketch, "E405", {"start": v(-70.75, 9.3) * mm, "end": v(-71.06, 9.06) * mm});
            skLineSegment(sketch, "E406", {"start": v(-71.06, 9.06) * mm, "end": v(-71.3, 8.75) * mm});
            skLineSegment(sketch, "E407", {"start": v(-71.3, 8.75) * mm, "end": v(-71.45, 8.39) * mm});
            skLineSegment(sketch, "E408", {"start": v(-71.45, 8.39) * mm, "end": v(-71.5, 8) * mm});
            skLineSegment(sketch, "E409", {"start": v(-101.3, 8.75) * mm, "end": v(-101.45, 8.39) * mm});
            skLineSegment(sketch, "E410", {"start": v(-101.45, 8.39) * mm, "end": v(-101.5, 8) * mm});
            skLineSegment(sketch, "E411", {"start": v(-101.5, 8) * mm, "end": v(-101.45, 7.61) * mm});
            skLineSegment(sketch, "E412", {"start": v(-101.45, 7.61) * mm, "end": v(-101.3, 7.25) * mm});
            skLineSegment(sketch, "E413", {"start": v(-101.3, 7.25) * mm, "end": v(-101.06, 6.94) * mm});
            skLineSegment(sketch, "E414", {"start": v(-101.06, 6.94) * mm, "end": v(-100.75, 6.7) * mm});
            skLineSegment(sketch, "E415", {"start": v(-100.75, 6.7) * mm, "end": v(-100.39, 6.55) * mm});
            skLineSegment(sketch, "E416", {"start": v(-100.39, 6.55) * mm, "end": v(-100, 6.5) * mm});
            skLineSegment(sketch, "E417", {"start": v(-100, 6.5) * mm, "end": v(-99.61, 6.55) * mm});
            skLineSegment(sketch, "E418", {"start": v(-99.61, 6.55) * mm, "end": v(-99.25, 6.7) * mm});
            skLineSegment(sketch, "E419", {"start": v(-99.25, 6.7) * mm, "end": v(-98.94, 6.94) * mm});
            skLineSegment(sketch, "E420", {"start": v(-98.94, 6.94) * mm, "end": v(-98.7, 7.25) * mm});
            skLineSegment(sketch, "E421", {"start": v(-98.7, 7.25) * mm, "end": v(-98.55, 7.61) * mm});
            skLineSegment(sketch, "E422", {"start": v(-98.55, 7.61) * mm, "end": v(-98.5, 8) * mm});
            skLineSegment(sketch, "E423", {"start": v(-98.5, 8) * mm, "end": v(-98.55, 8.39) * mm});
            skLineSegment(sketch, "E424", {"start": v(-98.55, 8.39) * mm, "end": v(-98.7, 8.75) * mm});
            skLineSegment(sketch, "E425", {"start": v(-98.7, 8.75) * mm, "end": v(-98.94, 9.06) * mm});
            skLineSegment(sketch, "E426", {"start": v(-98.94, 9.06) * mm, "end": v(-99.25, 9.3) * mm});
            skLineSegment(sketch, "E427", {"start": v(-99.25, 9.3) * mm, "end": v(-99.61, 9.45) * mm});
            skLineSegment(sketch, "E428", {"start": v(-99.61, 9.45) * mm, "end": v(-100, 9.5) * mm});
            skLineSegment(sketch, "E429", {"start": v(-100, 9.5) * mm, "end": v(-100.39, 9.45) * mm});
            skLineSegment(sketch, "E430", {"start": v(-100.39, 9.45) * mm, "end": v(-100.75, 9.3) * mm});
            skLineSegment(sketch, "E431", {"start": v(-100.75, 9.3) * mm, "end": v(-101.06, 9.06) * mm});
            skLineSegment(sketch, "E432", {"start": v(-101.06, 9.06) * mm, "end": v(-101.3, 8.75) * mm});
            skCircle(sketch, "E433", {"center": v(192.5, -7) * mm, "radius": 1.5 * mm});
            skCircle(sketch, "E434", {"center": v(-192.5, -7) * mm, "radius": 1.5 * mm});
            skCircle(sketch, "E435", {"center": v(-85, 8) * mm, "radius": 4 * mm});
            skCircle(sketch, "E436", {"center": v(85, 8) * mm, "radius": 4 * mm});
            skCircle(sketch, "E437", {"center": v(0, 8) * mm, "radius": 12 * mm});
            skSolve(sketch);
        }
        {
            var Q0;
            Q0=makeQuery(id+"F2.imprint","IMPRINT",FACE,{"disambiguationData":[TD([[makeQuery(id+"F2.imprint","IMPRINT",EDGE,{"derivedFrom":sQuery(id+"F2.wireOp",EDGE,"E17")}),-1.0]])]});
            extrude(context, id + "F3", {"entities" : qUnion([Q0]), "depth" : 15 * mm});
        }
        {
            var Q0;
            Q0=qCreatedBy(makeId("Front.planeOp"),FACE);
            var sketch = newSketch(context, id + "F4", { "sketchPlane" : qUnion([Q0])});
            skLineSegment(sketch, "E438", {"start": v(30, -185) * mm, "end": v(-30, -185) * mm});
            skLineSegment(sketch, "E439", {"start": v(-30, -185) * mm, "end": v(-30, 185) * mm});
            skLineSegment(sketch, "E440", {"start": v(-30, 185) * mm, "end": v(30, 185) * mm});
            skLineSegment(sketch, "E441", {"start": v(30, 185) * mm, "end": v(30, -185) * mm});
            skLineSegment(sketch, "E442", {"start": v(3.86, -51.04) * mm, "end": v(4, -50) * mm});
            skLineSegment(sketch, "E443", {"start": v(4, -50) * mm, "end": v(4, 150) * mm});
            skLineSegment(sketch, "E444", {"start": v(4, 150) * mm, "end": v(3.86, 151.04) * mm});
            skLineSegment(sketch, "E445", {"start": v(3.86, 151.04) * mm, "end": v(3.46, 152) * mm});
            skLineSegment(sketch, "E446", {"start": v(3.46, 152) * mm, "end": v(2.83, 152.83) * mm});
            skLineSegment(sketch, "E447", {"start": v(2.83, 152.83) * mm, "end": v(2, 153.46) * mm});
            skLineSegment(sketch, "E448", {"start": v(2, 153.46) * mm, "end": v(1.04, 153.86) * mm});
            skLineSegment(sketch, "E449", {"start": v(1.04, 153.86) * mm, "end": v(0, 154) * mm});
            skLineSegment(sketch, "E450", {"start": v(0, 154) * mm, "end": v(-1.04, 153.86) * mm});
            skLineSegment(sketch, "E451", {"start": v(-1.04, 153.86) * mm, "end": v(-2, 153.46) * mm});
            skLineSegment(sketch, "E452", {"start": v(-2, 153.46) * mm, "end": v(-2.83, 152.83) * mm});
            skLineSegment(sketch, "E453", {"start": v(-2.83, 152.83) * mm, "end": v(-3.46, 152) * mm});
            skLineSegment(sketch, "E454", {"start": v(-3.46, 152) * mm, "end": v(-3.86, 151.04) * mm});
            skLineSegment(sketch, "E455", {"start": v(-3.86, 151.04) * mm, "end": v(-4, 150) * mm});
            skLineSegment(sketch, "E456", {"start": v(-4, 150) * mm, "end": v(-4, -50) * mm});
            skLineSegment(sketch, "E457", {"start": v(-4, -50) * mm, "end": v(-3.86, -51.04) * mm});
            skLineSegment(sketch, "E458", {"start": v(-3.86, -51.04) * mm, "end": v(-3.46, -52) * mm});
            skLineSegment(sketch, "E459", {"start": v(-3.46, -52) * mm, "end": v(-2.83, -52.83) * mm});
            skLineSegment(sketch, "E460", {"start": v(-2.83, -52.83) * mm, "end": v(-2, -53.46) * mm});
            skLineSegment(sketch, "E461", {"start": v(-2, -53.46) * mm, "end": v(-1.04, -53.86) * mm});
            skLineSegment(sketch, "E462", {"start": v(-1.04, -53.86) * mm, "end": v(0, -54) * mm});
            skLineSegment(sketch, "E463", {"start": v(0, -54) * mm, "end": v(1.04, -53.86) * mm});
            skLineSegment(sketch, "E464", {"start": v(1.04, -53.86) * mm, "end": v(2, -53.46) * mm});
            skLineSegment(sketch, "E465", {"start": v(2, -53.46) * mm, "end": v(2.83, -52.83) * mm});
            skLineSegment(sketch, "E466", {"start": v(2.83, -52.83) * mm, "end": v(3.46, -52) * mm});
            skLineSegment(sketch, "E467", {"start": v(3.46, -52) * mm, "end": v(3.86, -51.04) * mm});
            skSolve(sketch);
        }
        {
            var Q0;
            Q0=makeQuery(id+"F4.imprint","IMPRINT",FACE,{"disambiguationData":[TD([[makeQuery(id+"F4.imprint","IMPRINT",EDGE,{"derivedFrom":sQuery(id+"F4.wireOp",EDGE,"E438")}),-1.0]])]});
            extrude(context, id + "F5", {"entities" : qUnion([Q0]), "depth" : 15 * mm});
        }
    });
